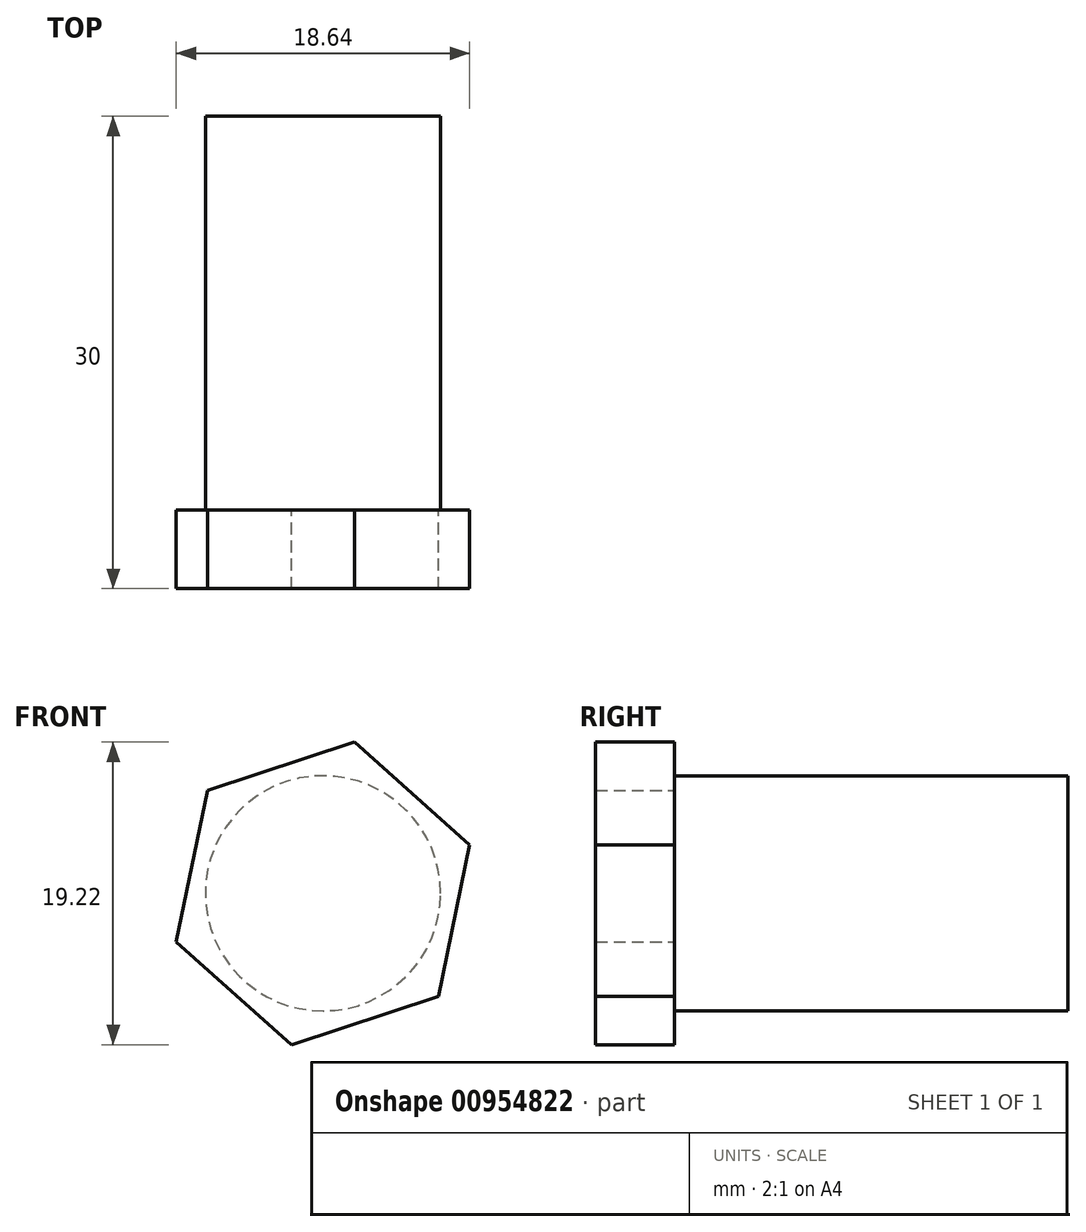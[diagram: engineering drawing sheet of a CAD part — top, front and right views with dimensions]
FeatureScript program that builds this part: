
annotation { "Feature Type Name" : "Feature", "Feature Type Description" : "" }
export const myFeature = defineFeature(function(context is Context, id is Id, definition is map)
    precondition{}
    {
        {
            var Q0;
            Q0=qCreatedBy(makeId("Front.planeOp"),FACE);
            var sketch = newSketch(context, id + "F0", { "sketchPlane" : qUnion([Q0])});
            skCircle(sketch, "E0.cCircle", {"center": v(0, 0) * mm, "radius": 8.5 * mm, "construction": true});
            skLineSegment(sketch, "E0.0", {"start": v(2, 9.61) * mm, "end": v(9.32, 3.08) * mm});
            skLineSegment(sketch, "E0.1", {"start": v(9.32, 3.08) * mm, "end": v(7.33, -6.53) * mm});
            skLineSegment(sketch, "E0.2", {"start": v(7.33, -6.53) * mm, "end": v(-2, -9.61) * mm});
            skLineSegment(sketch, "E0.3", {"start": v(-2, -9.61) * mm, "end": v(-9.32, -3.08) * mm});
            skLineSegment(sketch, "E0.4", {"start": v(-9.32, -3.08) * mm, "end": v(-7.33, 6.53) * mm});
            skLineSegment(sketch, "E0.5", {"start": v(-7.33, 6.53) * mm, "end": v(2, 9.61) * mm});
            skPoint(sketch, "E0.0.midPoint", {"position": v(5.65, 6.35) * mm});
            skSolve(sketch);
        }
        {
            var Q0;
            Q0=makeQuery(id+"F0.imprint","IMPRINT",FACE,{"disambiguationData":[TD([[makeQuery(id+"F0.imprint","IMPRINT",EDGE,{"derivedFrom":sQuery(id+"F0.wireOp",EDGE,"E0.0")}),-1.0]])]});
            extrude(context, id + "F1", {"entities" : qUnion([Q0]), "depth" : 5 * mm, "offsetDistance" : 25 * mm});
        }
        {
            var Q0;
            Q0=makeQuery(id+"F1.opExtrude","CAP_FACE",FACE,{"disambiguationData":[OSD([sQuery(id+"F0.wireOp",EDGE,"E0.0"),sQuery(id+"F0.wireOp",EDGE,"E0.1"),sQuery(id+"F0.wireOp",EDGE,"E0.2"),sQuery(id+"F0.wireOp",EDGE,"E0.3"),sQuery(id+"F0.wireOp",EDGE,"E0.4"),sQuery(id+"F0.wireOp",EDGE,"E0.5")])],"isStart":true});
            var sketch = newSketch(context, id + "F2", { "sketchPlane" : qUnion([Q0])});
            skCircle(sketch, "E1", {"center": v(0, 0) * mm, "radius": 7.47 * mm});
            skSolve(sketch);
        }
        {
            var Q0;
            Q0 = qSketchRegion(id + "F2", true);
            extrude(context, id + "F3", {"entities" : qUnion([Q0]), "operationType" : NewBodyOperationType.ADD, "depth" : 25 * mm, "offsetDistance" : 25 * mm});
        }
    });
